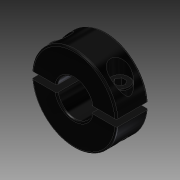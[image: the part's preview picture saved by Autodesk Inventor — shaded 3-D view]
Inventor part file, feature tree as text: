
AUTODESK INVENTOR PART (.ipt)
format: ipt  version: 2015 (Build 190159000, 159)  size: 2,283,008 bytes
history: native  units: in
note: dims shown in document units (in); Inventor stores cm internally (conversion verified against a paired STEP export)
features: other x4, imported_body x4, mirror x1
ambient origin geometry x8: Origin, YZ Plane, XZ Plane, XY Plane, X Axis, Y Axis, Z Axis, Center Point
bodies: Body1 (feature_tree), Body2 (feature_tree), Body3 (feature_tree), Body4 (feature_tree)
feature tree (9):
  mirror  "Mirror1"
  other  "6063K1501"
  other  "Cut-Sweep1"
  other  "LPattern1"
  other  "Cut-Extrude3"
  imported_body  "Base1"
  imported_body  "Base2"
  imported_body  "Base3"
  imported_body  "Base4"
